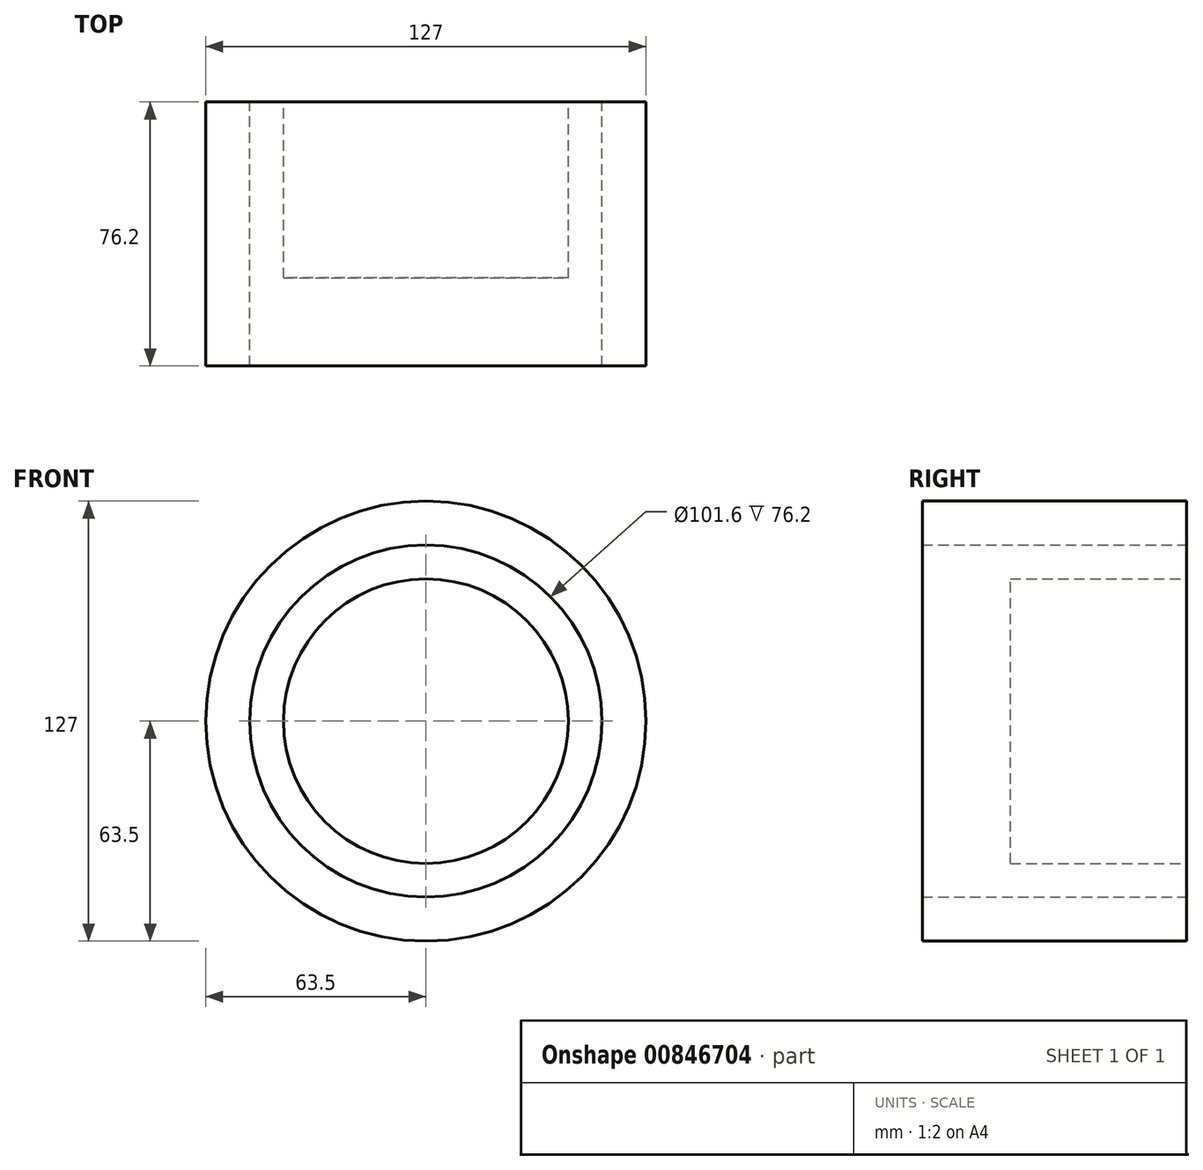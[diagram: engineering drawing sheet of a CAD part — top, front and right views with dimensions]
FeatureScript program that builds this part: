
annotation { "Feature Type Name" : "Feature", "Feature Type Description" : "" }
export const myFeature = defineFeature(function(context is Context, id is Id, definition is map)
    precondition{}
    {
        {
            var Q0;
            Q0=qCreatedBy(makeId("Front.planeOp"),FACE);
            var sketch = newSketch(context, id + "F0", { "sketchPlane" : qUnion([Q0])});
            skCircle(sketch, "E0", {"center": v(0, 0) * mm, "radius": 63.5 * mm});
            skCircle(sketch, "E1", {"center": v(0, 0) * mm, "radius": 50.8 * mm});
            skLineSegment(sketch, "E2.bottom", {"start": v(-22.41, 27.98) * mm, "end": v(28.39, 27.98) * mm});
            skLineSegment(sketch, "E2.top", {"start": v(-22.41, -22.82) * mm, "end": v(28.39, -22.82) * mm});
            skLineSegment(sketch, "E2.left", {"start": v(-22.41, 27.98) * mm, "end": v(-22.41, -22.82) * mm});
            skLineSegment(sketch, "E2.right", {"start": v(28.39, 27.98) * mm, "end": v(28.39, -22.82) * mm});
            skSolve(sketch);
        }
        {
            var Q0;
            Q0 = qSketchRegion(id + "Fwt8B6VqhBvKKUX_0", true);
            var Q1;
            Q1=makeQuery(id+"F0.imprint","IMPRINT",FACE,{"disambiguationData":[TD([[makeQuery(id+"F0.imprint","IMPRINT",EDGE,{"derivedFrom":sQuery(id+"F0.wireOp",EDGE,"E0")}),1.0]])]});
            extrude(context, id + "F1", {"entities" : qUnion([Q0, Q1]), "depth" : 50.8 * mm, "offsetDistance" : 25.4 * mm});
        }
        {
            var Q0;
            Q0=qCreatedBy(makeId("Front.planeOp"),FACE);
            var sketch = newSketch(context, id + "F2", { "sketchPlane" : qUnion([Q0])});
            skLineSegment(sketch, "E3.bottom", {"start": v(-25.4, 25.4) * mm, "end": v(25.4, 25.4) * mm});
            skLineSegment(sketch, "E3.top", {"start": v(-25.4, -25.4) * mm, "end": v(25.4, -25.4) * mm});
            skLineSegment(sketch, "E3.left", {"start": v(-25.4, 25.4) * mm, "end": v(-25.4, -25.4) * mm});
            skLineSegment(sketch, "E3.right", {"start": v(25.4, 25.4) * mm, "end": v(25.4, -25.4) * mm});
            skPoint(sketch, "E3.middle", {"position": v(0, 0) * mm});
            skSolve(sketch);
        }
        {
            var Q0;
            Q0=makeQuery(id+"F2.imprint","IMPRINT",FACE,{"disambiguationData":[TD([[makeQuery(id+"F2.imprint","IMPRINT",EDGE,{"derivedFrom":sQuery(id+"F2.wireOp",EDGE,"E3.bottom")}),-1.0]])]});
            extrude(context, id + "F3", {"entities" : qUnion([Q0]), "depth" : 50.8 * mm, "offsetDistance" : 25.4 * mm});
        }
        {
            var Q0;
            Q0=qCreatedBy(makeId("Front.planeOp"),FACE);
            var sketch = newSketch(context, id + "F4", { "sketchPlane" : qUnion([Q0])});
            skCircle(sketch, "E4", {"center": v(0, 0) * mm, "radius": 41.07 * mm});
            skSolve(sketch);
        }
        {
            var Q0;
            Q0=makeQuery(id+"F4.imprint","IMPRINT",FACE,{"disambiguationData":[TD([[makeQuery(id+"F4.imprint","IMPRINT",EDGE,{"derivedFrom":sQuery(id+"F4.wireOp",EDGE,"E4")}),1.0]])]});
            extrude(context, id + "F5", {"entities" : qUnion([Q0]), "operationType" : NewBodyOperationType.ADD, "depth" : 25.4 * mm, "offsetDistance" : 25.4 * mm});
        }
        {
            var Q0;
            Q0=makeQuery(id+"F1.opExtrude","CAP_FACE",FACE,{"disambiguationData":[OSD([sQuery(id+"F0.wireOp",EDGE,"E0"),sQuery(id+"F0.wireOp",EDGE,"E1")])],"isStart":false});
            extrude(context, id + "F6", {"entities" : qUnion([Q0]), "operationType" : NewBodyOperationType.ADD, "depth" : 25.4 * mm, "offsetDistance" : 25.4 * mm});
        }
        {
            var Q0;
            Q0=makeQuery(id+"F5.opExtrude","CAP_FACE",FACE,{"disambiguationData":[OSD([sQuery(id+"F4.wireOp",EDGE,"E4")])],"isStart":false});
            extrude(context, id + "F7", {"entities" : qUnion([Q0]), "operationType" : NewBodyOperationType.ADD, "depth" : 25.4 * mm, "offsetDistance" : 25.4 * mm});
        }
    });
